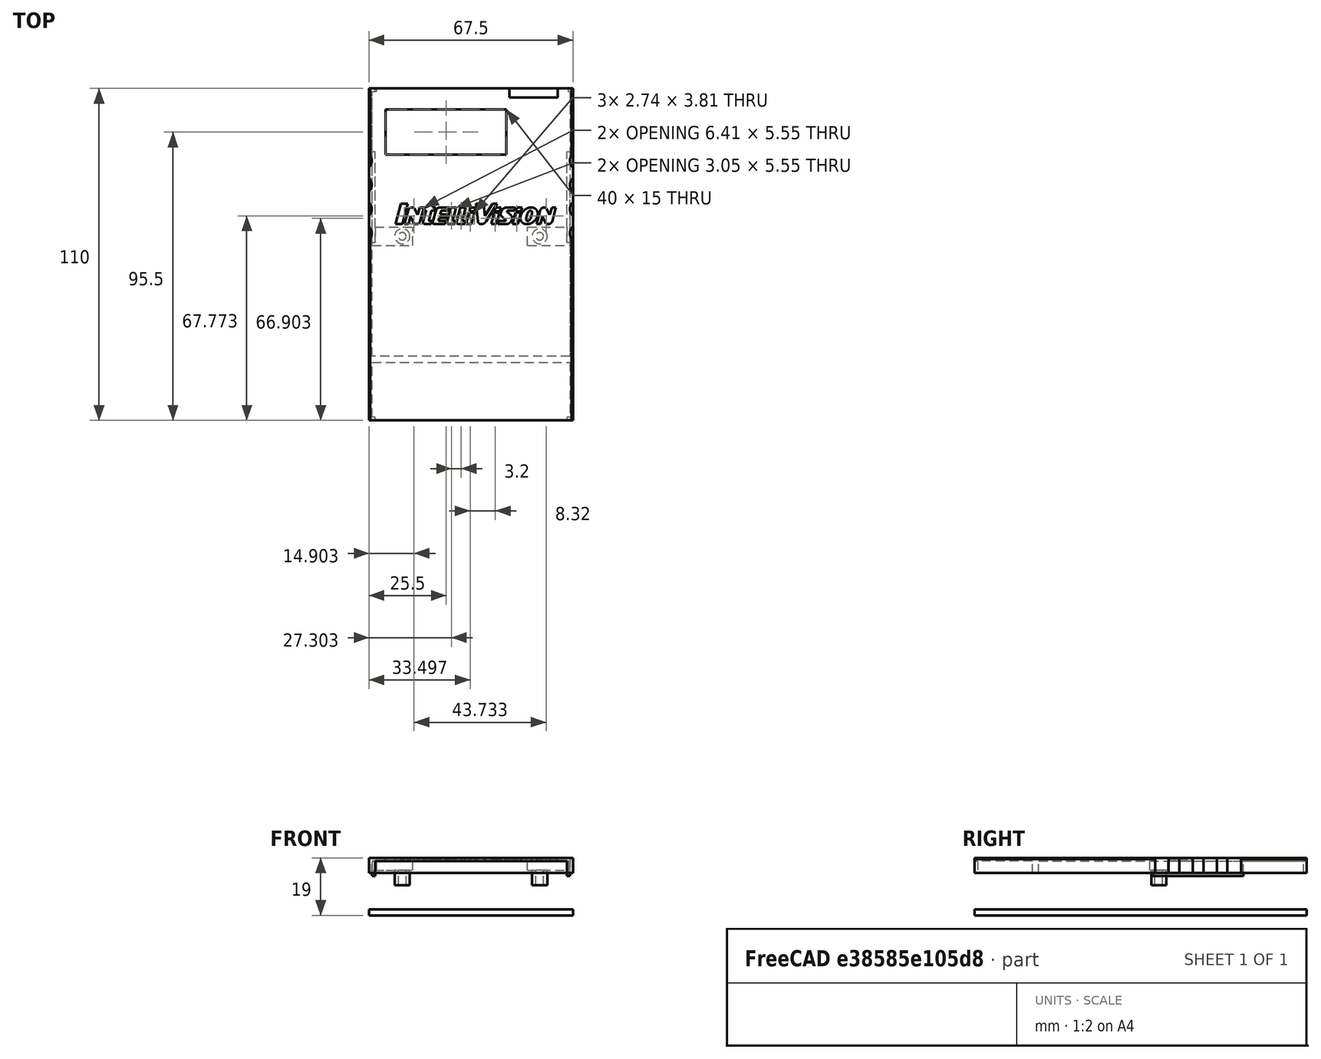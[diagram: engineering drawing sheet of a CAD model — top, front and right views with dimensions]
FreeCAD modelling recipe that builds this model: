
FCSTD DOCUMENT  (FreeCAD 0.20R29410 (Git))
Label: RTO_Cart_TOP
License: All rights reserved
LicenseURL: http://en.wikipedia.org/wiki/All_rights_reserved
objects: Part::Cut×12, Part::Cylinder×8, Part::Box×7, Part::MultiFuse×7, Sketcher::SketchObject×6, PartDesign::Pad×4, PartDesign::Pocket×2, PartDesign::Body×2, Part::FeaturePython×2, Part::Feature×2, Mesh::Feature×2, Part::Part2DObjectPython×1, Part::Extrusion×1, Part::Chamfer×1
note: 61 computed .brp shape members not serialized (recipe doc carries the construction recipe); baked Part::Feature solids carry a one-line shape summary decoded from their .brp

FEATURE [Sketcher::SketchObject] Sketch
  FullyConstrained = true
  MapMode = 5
  Support = -> [XY_Plane009]
  sketch-geometry (4):
    g0: LineSegment StartX=-67.5 StartY=110 StartZ=0 EndX=0 EndY=110 EndZ=0
    g1: LineSegment StartX=0 StartY=110 StartZ=0 EndX=0 EndY=0 EndZ=0
    g2: LineSegment StartX=0 StartY=0 StartZ=0 EndX=-67.5 EndY=0 EndZ=0
    g3: LineSegment StartX=-67.5 StartY=0 StartZ=0 EndX=-67.5 EndY=110 EndZ=0
  constraints (12):
    c: Coincident(g0,g1)
    c: Coincident(g1,g2)
    c: Coincident(g2,g3)
    c: Coincident(g3,g0)
    c: Horizontal(g0)
    c: Horizontal(g2)
    c: Vertical(g1)
    c: Vertical(g3)
    c: DistanceX(g0,g0) = 67.5
    c: DistanceY(g1,g1) = 110
    c: DistanceX(g-1,g1) = 0
    c: DistanceY(g1,g-1) = 0
FEATURE [PartDesign::Pad] Pad
  Direction = (0,0,1)
  Length = 2
  Length2 = 10
  Profile = -> Sketch
  ReferenceAxis = -> Sketch [N_Axis]
  Type = 0
FEATURE [Sketcher::SketchObject] Sketch009
  FullyConstrained = true
  Placement = pos=(0,0,10) rot=(0,0,-1;0rad)
  sketch-geometry (8):
    g0: LineSegment StartX=-67.5 StartY=110 StartZ=0 EndX=0 EndY=110 EndZ=0
    g1: LineSegment StartX=0 StartY=110 StartZ=0 EndX=0 EndY=0 EndZ=0
    g2: LineSegment StartX=0 StartY=0 StartZ=0 EndX=-67.5 EndY=0 EndZ=0
    g3: LineSegment StartX=-67.5 StartY=0 StartZ=0 EndX=-67.5 EndY=110 EndZ=0
    g4: LineSegment StartX=-66.5 StartY=109 StartZ=0 EndX=-1 EndY=109 EndZ=0
    g5: LineSegment StartX=-1 StartY=109 StartZ=0 EndX=-1 EndY=1 EndZ=0
    g6: LineSegment StartX=-1 StartY=1 StartZ=0 EndX=-66.5 EndY=1 EndZ=0
    g7: LineSegment StartX=-66.5 StartY=1 StartZ=0 EndX=-66.5 EndY=109 EndZ=0
  constraints (24):
    c: Coincident(g0,g1)
    c: Coincident(g1,g2)
    c: Coincident(g2,g3)
    c: Coincident(g3,g0)
    c: Horizontal(g0)
    c: Horizontal(g2)
    c: Vertical(g1)
    c: Vertical(g3)
    c: DistanceX(g0,g0) = 67.5
    c: DistanceY(g1,g1) = 110
    c: DistanceX(g-1,g1) = 0
    c: DistanceY(g1,g-1) = 0
    c: Coincident(g4,g5)
    c: Coincident(g5,g6)
    c: Coincident(g6,g7)
    c: Coincident(g7,g4)
    c: Horizontal(g4)
    c: Horizontal(g6)
    c: Vertical(g5)
    c: Vertical(g7)
    c: DistanceX(g4,g0) = 1
    c: DistanceY(g4,g0) = 1
    c: DistanceY(g2,g6) = 1
    c: DistanceX(g2,g6) = 1
FEATURE [PartDesign::Pad] Pad007  label="frameTop"
  Direction = (0,0,1)
  Length = 5
  Length2 = 10
  Placement = pos=(0,0,10) rot=(0,0,-1;0rad)
  Profile = -> Sketch009
  ReferenceAxis = -> Sketch009 [N_Axis]
  Type = 0
FEATURE [Sketcher::SketchObject] Sketch011
  AttachmentOffset = pos=(0,0,2) rot=(0,0,1;0rad)
  FullyConstrained = true
  MapMode = 5
  Placement = pos=(0,0,2) rot=(0,0,1;0rad)
  Support = -> [XY_Plane003]
  sketch-geometry (4):
    g0: LineSegment StartX=-65.5 StartY=4 StartZ=0 EndX=-2 EndY=4 EndZ=0
    g1: LineSegment StartX=-2 StartY=4 StartZ=0 EndX=-2 EndY=-1.08 EndZ=0
    g2: LineSegment StartX=-2 StartY=-1.08 StartZ=0 EndX=-65.5 EndY=-1.08 EndZ=0
    g3: LineSegment StartX=-65.5 StartY=-1.08 StartZ=0 EndX=-65.5 EndY=4 EndZ=0
  constraints (12):
    c: Coincident(g0,g1)
    c: Coincident(g1,g2)
    c: Coincident(g2,g3)
    c: Coincident(g3,g0)
    c: Horizontal(g0)
    c: Horizontal(g2)
    c: Vertical(g1)
    c: Vertical(g3)
    c: DistanceX(g0) = -2
    c: DistanceX(g0,g0) = 63.5
    c: DistanceY(g-1,g0) = 4
    c: DistanceY(g3,g3) = 5.08
FEATURE [PartDesign::Pocket] Pocket002
  BaseFeature = -> Pad007
  Direction = (0,0,-1)
  Length = 14
  Length2 = 5
  Placement = pos=(0,0,10) rot=(0,0,-1;0rad)
  Profile = -> Sketch011
  ReferenceAxis = -> Sketch011 [N_Axis]
  Reversed = true
  Type = 0
FEATURE [Sketcher::SketchObject] Sketch018
  AttachmentOffset = pos=(0,0,14) rot=(0,0,1;0rad)
  FullyConstrained = true
  MapMode = 5
  Placement = pos=(0,0,14) rot=(0,0,1;0rad)
  Support = -> [XY_Plane003]
  sketch-geometry (4):
    g0: LineSegment StartX=-67.5 StartY=0 StartZ=0 EndX=0 EndY=0 EndZ=0
    g1: LineSegment StartX=0 StartY=0 StartZ=0 EndX=0 EndY=110 EndZ=0
    g2: LineSegment StartX=0 StartY=110 StartZ=0 EndX=-67.5 EndY=110 EndZ=0
    g3: LineSegment StartX=-67.5 StartY=110 StartZ=0 EndX=-67.5 EndY=0 EndZ=0
  constraints (11):
    c: Coincident(g0,g1)
    c: Coincident(g1,g2)
    c: Coincident(g2,g3)
    c: Coincident(g3,g0)
    c: Horizontal(g0)
    c: Vertical(g1)
    c: Vertical(g3)
    c: DistanceY(g1,g1) = 110
    c: Horizontal(g2)
    c: Coincident(g-1,g0)
    c: DistanceX(g0,g0) = 67.5
FEATURE [Sketcher::SketchObject] Sketch019
  AttachmentOffset = pos=(0,0,14) rot=(0,0,1;0rad)
  FullyConstrained = true
  MapMode = 5
  Placement = pos=(0,0,14) rot=(0,0,1;0rad)
  Support = -> [XY_Plane003]
  sketch-geometry (4):
    g0: LineSegment StartX=-67.5 StartY=19.2 StartZ=0 EndX=0 EndY=19.2 EndZ=0
    g1: LineSegment StartX=0 StartY=19.2 StartZ=0 EndX=0 EndY=21.2 EndZ=0
    g2: LineSegment StartX=0 StartY=21.2 StartZ=0 EndX=-67.5 EndY=21.2 EndZ=0
    g3: LineSegment StartX=-67.5 StartY=21.2 StartZ=0 EndX=-67.5 EndY=19.2 EndZ=0
  constraints (12):
    c: Coincident(g0,g1)
    c: Coincident(g1,g2)
    c: Coincident(g2,g3)
    c: Coincident(g3,g0)
    c: Horizontal(g0)
    c: Horizontal(g2)
    c: Vertical(g1)
    c: Vertical(g3)
    c: DistanceY(g1,g1) = 2
    c: DistanceX(g0,g0) = 67.5
    c: DistanceX(g-1,g0) = 0
    c: DistanceY(g-1,g0) = 19.2
FEATURE [PartDesign::Pad] Pad011  label="barra_h"
  BaseFeature = -> Pocket002
  Direction = (0,0,1)
  Length = 4
  Length2 = 10
  Placement = pos=(0,0,10) rot=(0,0,-1;0rad)
  Profile = -> Sketch019
  ReferenceAxis = -> Sketch019 [N_Axis]
  Reversed = true
  Type = 0
FEATURE [Sketcher::SketchObject] Sketch021
  FullyConstrained = false
  MapMode = 5
  Support = -> [XY_Plane003]
  sketch-geometry (4):
    g0: LineSegment StartX=-1.62421 StartY=137.927 StartZ=0 EndX=-65.1242 EndY=137.927 EndZ=0
    g1: LineSegment StartX=-65.1242 StartY=137.927 StartZ=0 EndX=-65.1242 EndY=27.927 EndZ=0
    g2: LineSegment StartX=-65.1242 StartY=27.927 StartZ=0 EndX=-1.62421 EndY=27.927 EndZ=0
    g3: LineSegment StartX=-1.62421 StartY=27.927 StartZ=0 EndX=-1.62421 EndY=137.927 EndZ=0
  constraints (10):
    c: Coincident(g0,g1)
    c: Coincident(g1,g2)
    c: Coincident(g2,g3)
    c: Coincident(g3,g0)
    c: Horizontal(g0)
    c: Horizontal(g2)
    c: Vertical(g1)
    c: Vertical(g3)
    c: DistanceY(g1,g1) = 110
    c: DistanceX(g0,g0) = 63.5
FEATURE [PartDesign::Pocket] Pocket004
  BaseFeature = -> Pad011
  Direction = (0,0,-1)
  Length = 26
  Length2 = 5
  Placement = pos=(0,0,10) rot=(0,0,-1;0rad)
  Profile = -> Sketch021
  ReferenceAxis = -> Sketch021 [N_Axis]
  Reversed = true
  Type = 0
FEATURE [PartDesign::Body] Body
  Group = -> [Sketch,Pad]
  Origin = -> Origin007
  Tip = -> Pad
FEATURE [Part::FeaturePython] Tube  # WARN: FeaturePython — macro-defined, semantics opaque (R4)
  AttacherType = Attacher::AttachEngine3D
  Height = 8
  InnerRadius = 1.25
  OuterRadius = 2.5
  Placement = pos=(-11,61,10) rot=(0,0,1;0rad)
FEATURE [Part::FeaturePython] Tube001  # WARN: FeaturePython — macro-defined, semantics opaque (R4)
  AttacherType = Attacher::AttachEngine3D
  Height = 8
  InnerRadius = 1.25
  OuterRadius = 2.5
  Placement = pos=(-56.5,61,10) rot=(0,0,1;0rad)
FEATURE [Part::Cylinder] Cylinder003  label="Cilindro002"
  Angle = 360
  AttacherType = Attacher::AttachEngine3D
  FirstAngle = 0
  Height = 22
  Placement = pos=(2,62,9) rot=(0,0,1;0rad)
  Radius = 3
  SecondAngle = 0
FEATURE [Part::Cylinder] Cylinder004  label="Cilindro003"
  Angle = 360
  AttacherType = Attacher::AttachEngine3D
  FirstAngle = 0
  Height = 22
  Placement = pos=(2,70,9) rot=(0,0,1;0rad)
  Radius = 3
  SecondAngle = 0
FEATURE [Part::Cylinder] Cylinder005  label="Cilindro004"
  Angle = 360
  AttacherType = Attacher::AttachEngine3D
  FirstAngle = 0
  Height = 22
  Placement = pos=(2,78,9) rot=(0,0,1;0rad)
  Radius = 3
  SecondAngle = 0
FEATURE [Part::Cylinder] Cylinder006  label="Cilindro005"
  Angle = 360
  AttacherType = Attacher::AttachEngine3D
  FirstAngle = 0
  Height = 22
  Placement = pos=(2,86,9) rot=(0,0,1;0rad)
  Radius = 3
  SecondAngle = 0
FEATURE [Part::Cylinder] Cylinder007  label="Cilindro006"
  Angle = 360
  AttacherType = Attacher::AttachEngine3D
  FirstAngle = 0
  Height = 22
  Placement = pos=(-69.6,62,9) rot=(0,0,1;0rad)
  Radius = 3
  SecondAngle = 0
FEATURE [Part::Cylinder] Cylinder008  label="Cilindro007"
  Angle = 360
  AttacherType = Attacher::AttachEngine3D
  FirstAngle = 0
  Height = 22
  Placement = pos=(-69.6,70,9) rot=(0,0,1;0rad)
  Radius = 3
  SecondAngle = 0
FEATURE [Part::Cylinder] Cylinder009  label="Cilindro008"
  Angle = 360
  AttacherType = Attacher::AttachEngine3D
  FirstAngle = 0
  Height = 22
  Placement = pos=(-69.6,78,9) rot=(0,0,1;0rad)
  Radius = 3
  SecondAngle = 0
FEATURE [Part::Cylinder] Cylinder010  label="Cilindro009"
  Angle = 360
  AttacherType = Attacher::AttachEngine3D
  FirstAngle = 0
  Height = 22
  Placement = pos=(-69.6,86,9) rot=(0,0,1;0rad)
  Radius = 3
  SecondAngle = 0
FEATURE [PartDesign::Pad] Pad012
  BaseFeature = -> Pocket004
  Direction = (0,0,1)
  Length = 1
  Length2 = 10
  Placement = pos=(0,0,10) rot=(0,0,-1;0rad)
  Profile = -> Sketch018
  ReferenceAxis = -> Sketch018 [N_Axis]
  Type = 0
FEATURE [PartDesign::Body] Body002  label="TOP"
  Group = -> [Sketch009,Pad007,Sketch011,Pocket002,Sketch018,Sketch019,Pad011,Sketch021,Pocket004,Pad012]
  Origin = -> Origin002
  Placement = pos=(0,0,4) rot=(0,0,1;0rad)
  Tip = -> Pad012
FEATURE [Part::Box] Box001  label="Cubo001"
  AttacherType = Attacher::AttachEngine3D
  Height = 10
  Length = 16
  Placement = pos=(-21,107,13) rot=(0,0,1;0rad)
  Width = 5
FEATURE [Part::Box] Box002  label="Cubo002"
  AttacherType = Attacher::AttachEngine3D
  Height = 11
  Length = 64
  Placement = pos=(-65.5,105,7) rot=(0,0,1;0rad)
  Width = 7
FEATURE [Part::Box] Box003  label="Cubo003"
  AttacherType = Attacher::AttachEngine3D
  Height = 7
  Length = 40
  Placement = pos=(-62,88,15) rot=(0,0,1;0rad)
  Width = 15
FEATURE [Part::Part2DObjectPython] ShapeString  # Draft 2D object (typed FeaturePython)
  FontFile = <userpath>/Documents/Retrocomputer/Intellivision/3DModel/sfintell.ttf
  MakeFace = true
  Size = 4
  String = IntelliVision
  Tracking = 0
FEATURE [Part::Extrusion] Extrude
  Base = -> ShapeString
  Dir = (0,0,1)
  DirMode = 2
  FaceMakerClass = Part::FaceMakerBullseye
  LengthFwd = 4
  LengthRev = 0
  Placement = pos=(-59,65,18) rot=(0,0,1;0rad)
  Solid = false
  Symmetric = false
FEATURE [Part::Box] Box004  label="Cubo004"
  AttacherType = Attacher::AttachEngine3D
  Height = 5
  Length = 1
  Placement = pos=(-2,59,13) rot=(0,0,1;0rad)
  Width = 30
FEATURE [Part::Box] Box005  label="Cubo005"
  AttacherType = Attacher::AttachEngine3D
  Height = 5
  Length = 1
  Placement = pos=(-66.5,59,13) rot=(0,0,1;0rad)
  Width = 30
FEATURE [Part::Box] Box  label="Cubo"
  AttacherType = Attacher::AttachEngine3D
  Height = 3
  Length = 14
  Placement = pos=(-67,58,15) rot=(0,0,1;0rad)
  Width = 6
FEATURE [Part::Box] Box006  label="Cubo006"
  AttacherType = Attacher::AttachEngine3D
  Height = 3
  Length = 14
  Placement = pos=(-15,58,15) rot=(0,0,1;0rad)
  Width = 6
FEATURE [Part::MultiFuse] Fusion
  Shapes = -> [Tube001,Body002]
FEATURE [Part::MultiFuse] Fusion002
  Shapes = -> [Tube,Fusion]
FEATURE [Part::MultiFuse] Fusion003
  Shapes = -> [Fusion,Box004]
FEATURE [Part::MultiFuse] Fusion004
  Shapes = -> [Fusion002,Box005]
FEATURE [Part::MultiFuse] Fusion005
  Shapes = -> [Fusion003,Fusion004]
FEATURE [Part::Feature] Refined_Mesh_Solid_16203  label="RTO-Bottom"
  shape: bbox 67.5 x 110 x 10 mm, 370 faces, 0 solids (baked)
FEATURE [Mesh::Feature] Mesh  label="Bottom (Meshed)"
FEATURE [Part::Cut] Cut011
  Base = -> Body002
  Tool = -> Box002
FEATURE [Part::Cut] Cut
  Base = -> Fusion005
  Tool = -> Box003
FEATURE [Part::Cut] Cut012
  Base = -> Cut
  Tool = -> Box001
FEATURE [Part::MultiFuse] Fusion008
  Shapes = -> [Cut012,Box006]
FEATURE [Part::MultiFuse] Fusion009
  Shapes = -> [Fusion008,Box]
FEATURE [Part::Cut] Cut013
  Base = -> Fusion009
  Tool = -> Cylinder007
FEATURE [Part::Cut] Cut014
  Base = -> Cut013
  Tool = -> Cylinder008
FEATURE [Part::Cut] Cut015
  Base = -> Cut014
  Tool = -> Cylinder009
FEATURE [Part::Cut] Cut016
  Base = -> Cut015
  Tool = -> Cylinder010
FEATURE [Part::Cut] Cut017
  Base = -> Cut016
  Tool = -> Cylinder003
FEATURE [Part::Cut] Cut018
  Base = -> Cut017
  Tool = -> Cylinder004
FEATURE [Part::Cut] Cut019
  Base = -> Cut018
  Tool = -> Cylinder005
FEATURE [Part::Cut] Cut020
  Base = -> Cut019
  Tool = -> Cylinder006
FEATURE [Part::Cut] Cut021
  Base = -> Cut020
  Tool = -> Extrude
FEATURE [Part::Chamfer] Chamfer
  Base = -> Cut021
  Edges = 4 edges r=0.4: [Edge692,Edge696,Edge700,Edge711]
FEATURE [Mesh::Feature] Mesh001  label="Chamfer (Meshed)"
FEATURE [Part::Feature] Refined_Mesh001_Solid_54728
  shape: bbox 67.5 x 110 x 9 mm, 901 faces, 0 solids (baked)
